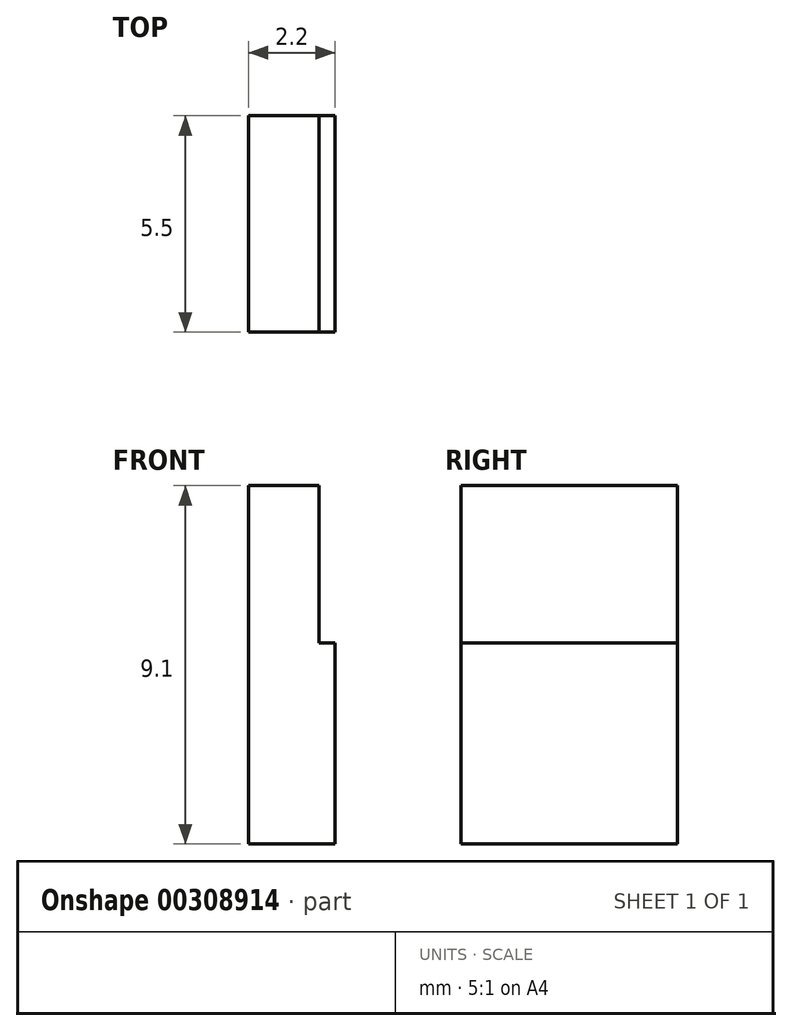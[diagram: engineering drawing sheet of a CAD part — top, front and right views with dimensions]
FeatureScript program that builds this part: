
annotation { "Feature Type Name" : "Feature", "Feature Type Description" : "" }
export const myFeature = defineFeature(function(context is Context, id is Id, definition is map)
    precondition{}
    {
        {
            var Q0;
            Q0=qCreatedBy(makeId("Front.planeOp"),FACE);
            var sketch = newSketch(context, id + "F0", { "sketchPlane" : qUnion([Q0])});
            skLineSegment(sketch, "E0", {"start": v(0, 0) * mm, "end": v(2.2, 0) * mm});
            skLineSegment(sketch, "E1", {"start": v(2.2, 0) * mm, "end": v(2.2, 5.1) * mm});
            skLineSegment(sketch, "E2", {"start": v(2.2, 5.1) * mm, "end": v(1.8, 5.1) * mm});
            skLineSegment(sketch, "E3", {"start": v(1.8, 5.1) * mm, "end": v(1.8, 9.1) * mm});
            skLineSegment(sketch, "E4", {"start": v(1.8, 9.1) * mm, "end": v(0, 9.1) * mm});
            skLineSegment(sketch, "E5", {"start": v(0, 9.1) * mm, "end": v(0, 0) * mm});
            skSolve(sketch);
        }
        {
            var Q0;
            Q0 = qSketchRegion(id + "F0", true);
            extrude(context, id + "F1", {"entities" : qUnion([Q0]), "depth" : 5.5 * mm});
        }
    });
